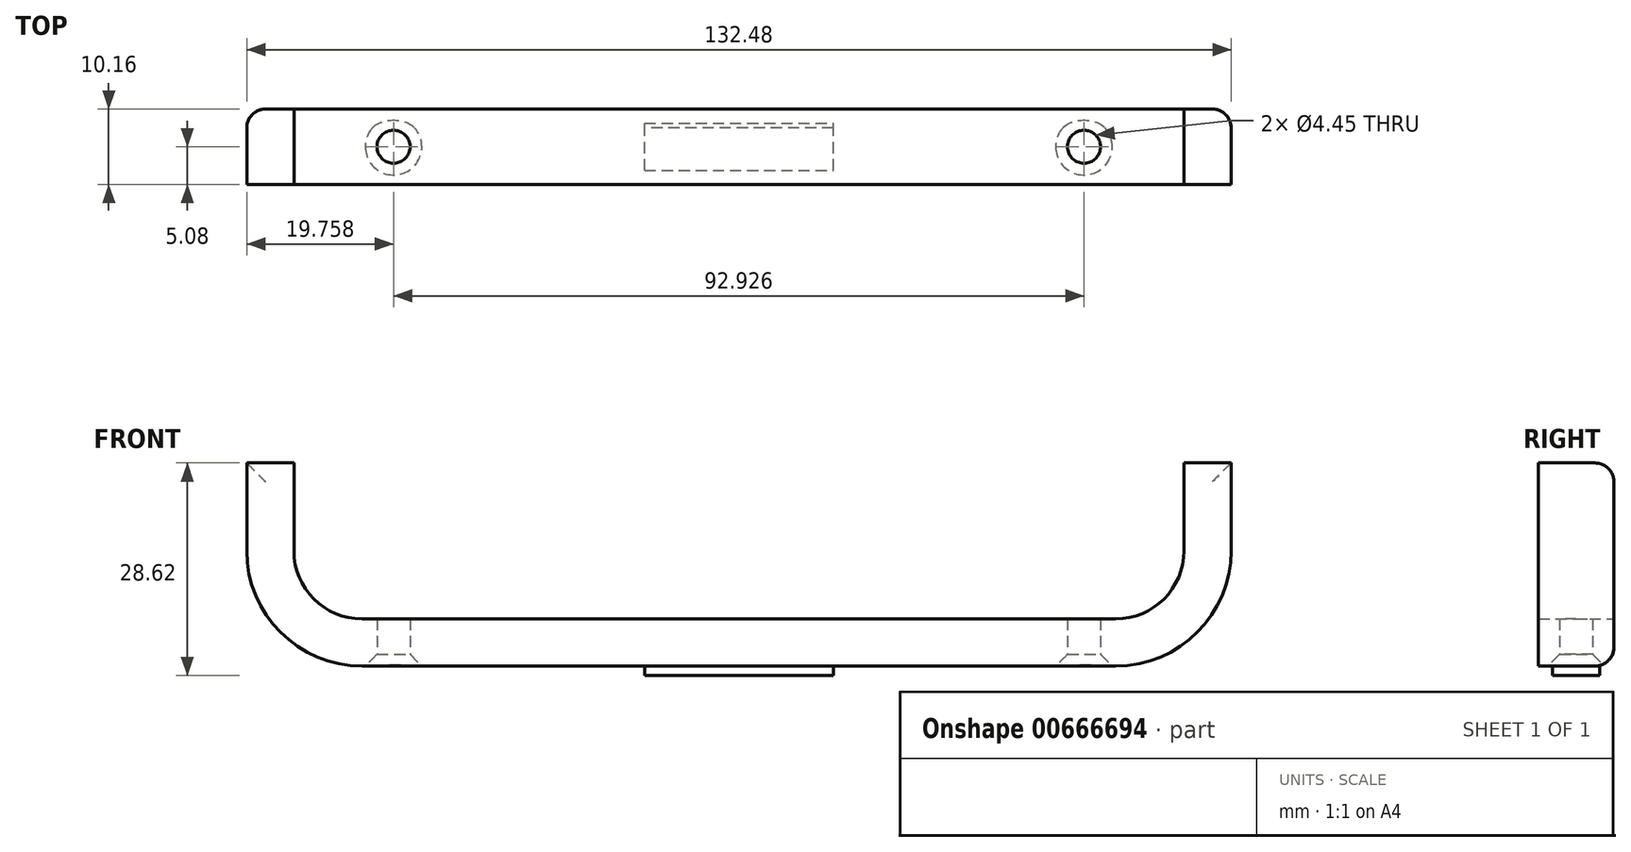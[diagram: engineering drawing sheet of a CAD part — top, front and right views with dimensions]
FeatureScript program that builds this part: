
annotation { "Feature Type Name" : "Feature", "Feature Type Description" : "" }
export const myFeature = defineFeature(function(context is Context, id is Id, definition is map)
    precondition{}
    {
        {
            var Q0;
            Q0=qCreatedBy(makeId("Front.planeOp"),FACE);
            var sketch = newSketch(context, id + "F0", { "sketchPlane" : qUnion([Q0])});
            skLineSegment(sketch, "E0", {"start": v(0, 0) * mm, "end": v(-50.71, 0) * mm});
            skArc(sketch, "E1", {"start": v(-50.71, 0) * mm, "mid": v(-57.2, 2.69) * mm, "end": v(-59.9, 9.18) * mm});
            skLineSegment(sketch, "E2", {"start": v(-59.9, 9.18) * mm, "end": v(-59.9, 21) * mm});
            skLineSegment(sketch, "E3.MirrorCS", {"start": v(59.9, 9.18) * mm, "end": v(59.9, 21) * mm});
            skArc(sketch, "E4.MirrorCS", {"start": v(50.71, 0) * mm, "mid": v(57.2, 2.69) * mm, "end": v(59.9, 9.18) * mm});
            skLineSegment(sketch, "E5.MirrorCS", {"start": v(0, 0) * mm, "end": v(50.71, 0) * mm});
            skLineSegment(sketch, "E6.0", {"start": v(66.24, 9.18) * mm, "end": v(66.24, 21) * mm});
            skArc(sketch, "E6.1", {"start": v(50.71, -6.35) * mm, "mid": v(61.7, -1.8) * mm, "end": v(66.24, 9.18) * mm});
            skLineSegment(sketch, "E6.2", {"start": v(-66.24, 9.18) * mm, "end": v(-66.24, 21) * mm});
            skArc(sketch, "E6.3", {"start": v(-50.71, -6.35) * mm, "mid": v(-61.7, -1.8) * mm, "end": v(-66.24, 9.18) * mm});
            skLineSegment(sketch, "E6.4", {"start": v(0, -6.35) * mm, "end": v(-50.71, -6.35) * mm});
            skLineSegment(sketch, "E6.5", {"start": v(0, -6.35) * mm, "end": v(50.71, -6.35) * mm});
            skLineSegment(sketch, "E7", {"start": v(-59.9, 21) * mm, "end": v(-66.24, 21) * mm});
            skLineSegment(sketch, "E8", {"start": v(66.24, 21) * mm, "end": v(59.9, 21) * mm});
            skSolve(sketch);
        }
        {
            var Q0;
            Q0=makeQuery(id+"F0.imprint","IMPRINT",FACE,{"disambiguationData":[TD([[makeQuery(id+"F0.imprint","IMPRINT",EDGE,{"derivedFrom":sQuery(id+"F0.wireOp",EDGE,"E0")}),1.0]])]});
            extrude(context, id + "F1", {"entities" : qUnion([Q0]), "endBound" : BoundingType.SYMMETRIC, "depth" : 10.16 * mm, "offsetDistance" : 25.4 * mm});
        }
        {
            var Q0;
            Q0=makeQuery(id+"F1.opExtrude","SWEPT_FACE",FACE,{"disambiguationData":[OSD([sQuery(id+"F0.wireOp",EDGE,"E6.4"),sQuery(id+"F0.wireOp",EDGE,"E6.5")])]});
            var sketch = newSketch(context, id + "F2", { "sketchPlane" : qUnion([Q0])});
            skCircle(sketch, "E9", {"center": v(46.44, 0) * mm, "radius": 4.05 * mm});
            skCircle(sketch, "E10", {"center": v(-46.48, 0) * mm, "radius": 4.05 * mm});
            skSolve(sketch);
        }
        {
            var Q0;
            Q0=sQuery(id+"F2.wireOp",VERTEX,"E10.center");
            var Q1;
            Q1=sQuery(id+"F2.wireOp",VERTEX,"E9.center");
            var Q2;
            Q2=makeQuery(id+"F1.opExtrude","SWEPT_BODY",BODY,{"disambiguationData":[OSD([sQuery(id+"F0.wireOp",EDGE,"E0"),sQuery(id+"F0.wireOp",EDGE,"E1"),sQuery(id+"F0.wireOp",EDGE,"E2"),sQuery(id+"F0.wireOp",EDGE,"E3.MirrorCS"),sQuery(id+"F0.wireOp",EDGE,"E4.MirrorCS"),sQuery(id+"F0.wireOp",EDGE,"E5.MirrorCS"),sQuery(id+"F0.wireOp",EDGE,"E6.0"),sQuery(id+"F0.wireOp",EDGE,"E6.1"),sQuery(id+"F0.wireOp",EDGE,"E6.2"),sQuery(id+"F0.wireOp",EDGE,"E6.3"),sQuery(id+"F0.wireOp",EDGE,"E6.4"),sQuery(id+"F0.wireOp",EDGE,"E6.5"),sQuery(id+"F0.wireOp",EDGE,"E7"),sQuery(id+"F0.wireOp",EDGE,"E8")])]});
            hole(context, id + "F3", {"style" : HoleStyle.C_SINK, "endStyle" : HoleEndStyle.THROUGH, "holeDiameter" : 4.44 * mm, "cSinkDiameter" : 7.62 * mm, "cSinkAngle" : 90 * degree, "majorDiameter" : 6.35 * mm, "isTappedThrough" : true, "tappedDepth" : 12.7 * mm, "tapClearance" : 3, "locations" : qUnion([Q0, Q1]), "scope" : qUnion([Q2])});
        }
        {
            var Q0;
            Q0=makeQuery(id+"F1.opExtrude","CAP_EDGE",EDGE,{"disambiguationData":[OSD([sQuery(id+"F0.wireOp",EDGE,"E6.4"),sQuery(id+"F0.wireOp",EDGE,"E6.5")])],"isStart":true});
            var Q1;
            Q1=makeQuery(id+"F1.opExtrude","CAP_EDGE",EDGE,{"disambiguationData":[OSD([sQuery(id+"F0.wireOp",EDGE,"E8")])],"isStart":true});
            var Q2;
            Q2=makeQuery(id+"F1.opExtrude","CAP_EDGE",EDGE,{"disambiguationData":[OSD([sQuery(id+"F0.wireOp",EDGE,"E7")])],"isStart":true});
            fillet(context, id + "F4", {"entities" : qUnion([Q0, Q1, Q2]), "radius" : 2.54 * mm, "tangentPropagation" : true, "allowEdgeOverflow" : false});
        }
        {
            var Q0;
            Q0=makeQuery(id+"F2.imprint","IMPRINT",FACE,{"disambiguationData":[TD([[makeQuery(id+"F2.imprint","IMPRINT",EDGE,{"derivedFrom":sQuery(id+"F2.wireOp",EDGE,"E9")}),-1.0]])]});
            var sketch = newSketch(context, id + "F5", { "sketchPlane" : qUnion([Q0])});
            skLineSegment(sketch, "E11.bottom", {"start": v(-12.7, 3.17) * mm, "end": v(12.7, 3.17) * mm});
            skLineSegment(sketch, "E11.top", {"start": v(-12.7, -3.17) * mm, "end": v(12.7, -3.17) * mm});
            skLineSegment(sketch, "E11.left", {"start": v(-12.7, 3.17) * mm, "end": v(-12.7, -3.17) * mm});
            skLineSegment(sketch, "E11.right", {"start": v(12.7, 3.17) * mm, "end": v(12.7, -3.17) * mm});
            skPoint(sketch, "E11.middle", {"position": v(0, 0) * mm});
            skSolve(sketch);
        }
        {
            var Q0;
            Q0=makeQuery(id+"F5.imprint","IMPRINT",FACE,{"disambiguationData":[TD([[makeQuery(id+"F5.imprint","IMPRINT",EDGE,{"derivedFrom":sQuery(id+"F5.wireOp",EDGE,"E11.bottom")}),-1.0]])]});
            extrude(context, id + "F6", {"entities" : qUnion([Q0]), "operationType" : NewBodyOperationType.ADD, "depth" : 1.27 * mm, "offsetDistance" : 25.4 * mm});
        }
    });
